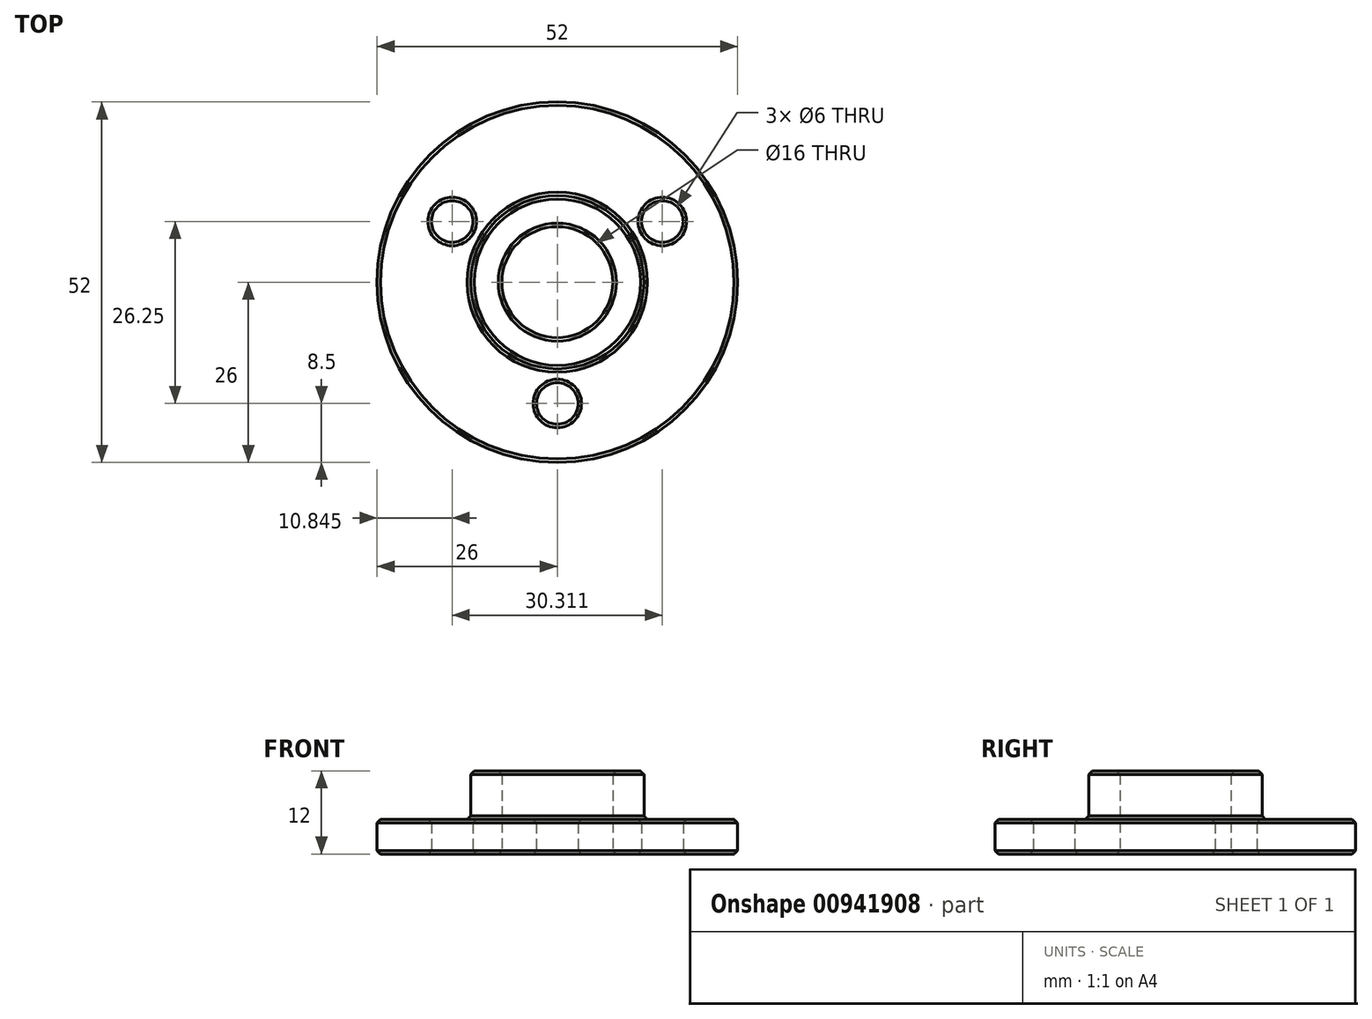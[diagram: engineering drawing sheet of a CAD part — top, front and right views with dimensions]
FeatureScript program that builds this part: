
annotation { "Feature Type Name" : "Feature", "Feature Type Description" : "" }
export const myFeature = defineFeature(function(context is Context, id is Id, definition is map)
    precondition{}
    {
        {
            var Q0;
            Q0=qCreatedBy(makeId("Top.planeOp"),FACE);
            var sketch = newSketch(context, id + "F0", { "sketchPlane" : qUnion([Q0])});
            skCircle(sketch, "E0", {"center": v(0, 0) * mm, "radius": 26 * mm});
            skCircle(sketch, "E1", {"center": v(0, 0) * mm, "radius": 12.5 * mm});
            skCircle(sketch, "E2", {"center": v(0, 0) * mm, "radius": 17.5 * mm, "construction": true});
            skPoint(sketch, "E3", {"position": v(0, -17.5) * mm});
            skLineSegment(sketch, "E4", {"start": v(0, 0) * mm, "end": v(-15.16, 8.75) * mm, "construction": true});
            skLineSegment(sketch, "E5", {"start": v(0, 0) * mm, "end": v(15.16, 8.75) * mm, "construction": true});
            skCircle(sketch, "E6", {"center": v(0, -17.5) * mm, "radius": 3 * mm});
            skCircle(sketch, "E7", {"center": v(-15.16, 8.75) * mm, "radius": 3 * mm});
            skCircle(sketch, "E8", {"center": v(15.16, 8.75) * mm, "radius": 3 * mm});
            skCircle(sketch, "E9", {"center": v(0, 0) * mm, "radius": 8 * mm});
            skSolve(sketch);
        }
        {
            var Q0;
            Q0=makeQuery(id+"F0.imprint","IMPRINT",FACE,{"disambiguationData":[TD([[makeQuery(id+"F0.imprint","IMPRINT",EDGE,{"derivedFrom":sQuery(id+"F0.wireOp",EDGE,"E0")}),1.0]])]});
            extrude(context, id + "F1", {"entities" : qUnion([Q0]), "depth" : 5 * mm, "offsetDistance" : 25 * mm});
        }
        {
            var Q0;
            Q0=makeQuery(id+"F0.imprint","IMPRINT",FACE,{"disambiguationData":[TD([[makeQuery(id+"F0.imprint","IMPRINT",EDGE,{"derivedFrom":sQuery(id+"F0.wireOp",EDGE,"E1")}),1.0]])]});
            extrude(context, id + "F2", {"entities" : qUnion([Q0]), "operationType" : NewBodyOperationType.ADD, "depth" : 12 * mm, "offsetDistance" : 25 * mm});
        }
        {
            var Q0;
            Q0=makeQuery(id+"F2.opExtrude","CAP_FACE",FACE,{"disambiguationData":[OSD([sQuery(id+"F0.wireOp",EDGE,"E1"),sQuery(id+"F0.wireOp",EDGE,"E9")])],"isStart":false});
            var Q1;
            Q1=makeQuery(id+"F1.opExtrude","CAP_FACE",FACE,{"disambiguationData":[OSD([sQuery(id+"F0.wireOp",EDGE,"E0"),sQuery(id+"F0.wireOp",EDGE,"E1"),sQuery(id+"F0.wireOp",EDGE,"E6"),sQuery(id+"F0.wireOp",EDGE,"E7"),sQuery(id+"F0.wireOp",EDGE,"E8")])],"isStart":false});
            var Q2;
            {var subQ0=sQuery(id+"F0.wireOp",EDGE,"E1");Q2=makeQuery(id+"F2.boolean.opBoolean","MERGE",FACE,{"derivedFrom":[makeQuery(id+"F1.opExtrude","CAP_FACE",FACE,{"disambiguationData":[OSD([sQuery(id+"F0.wireOp",EDGE,"E0"),subQ0,sQuery(id+"F0.wireOp",EDGE,"E6"),sQuery(id+"F0.wireOp",EDGE,"E7"),sQuery(id+"F0.wireOp",EDGE,"E8")])],"isStart":true}),makeQuery(id+"F2.opExtrude","CAP_FACE",FACE,{"disambiguationData":[OSD([subQ0,sQuery(id+"F0.wireOp",EDGE,"E9")])],"isStart":true})]});}
            chamfer(context, id + "F3", {"entities" : qUnion([Q0, Q1, Q2]), "width" : 0.5 * mm, "tangentPropagation" : true});
        }
    });
